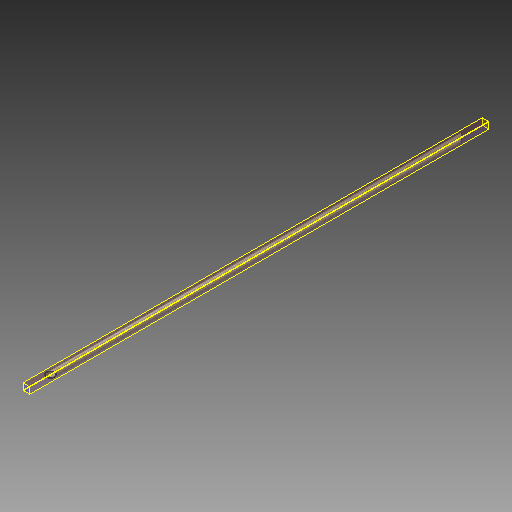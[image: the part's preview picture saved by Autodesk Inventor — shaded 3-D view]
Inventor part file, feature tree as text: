
AUTODESK INVENTOR PART (.ipt)
format: ipt  version: 2018 (Build 220112000, 112)  size: 104,960 bytes
history: native  units: mm
features: other x6, extrude x1, sketch x1
ambient origin geometry x8: Origin, YZ Plane, XZ Plane, XY Plane, X Axis, Y Axis, Z Axis, Center Point
bodies: Body1 (feature_tree)
feature tree (8):
  extrude  "押し出し2"  Depth=27.2mm
  other  "面の勾配1"
  other  "面の勾配2"
  other  "作業平面2"
  other  "作業平面4"
  other  "作業平面5"
  other  "作業平面6"
  sketch  "スケッチ3"
